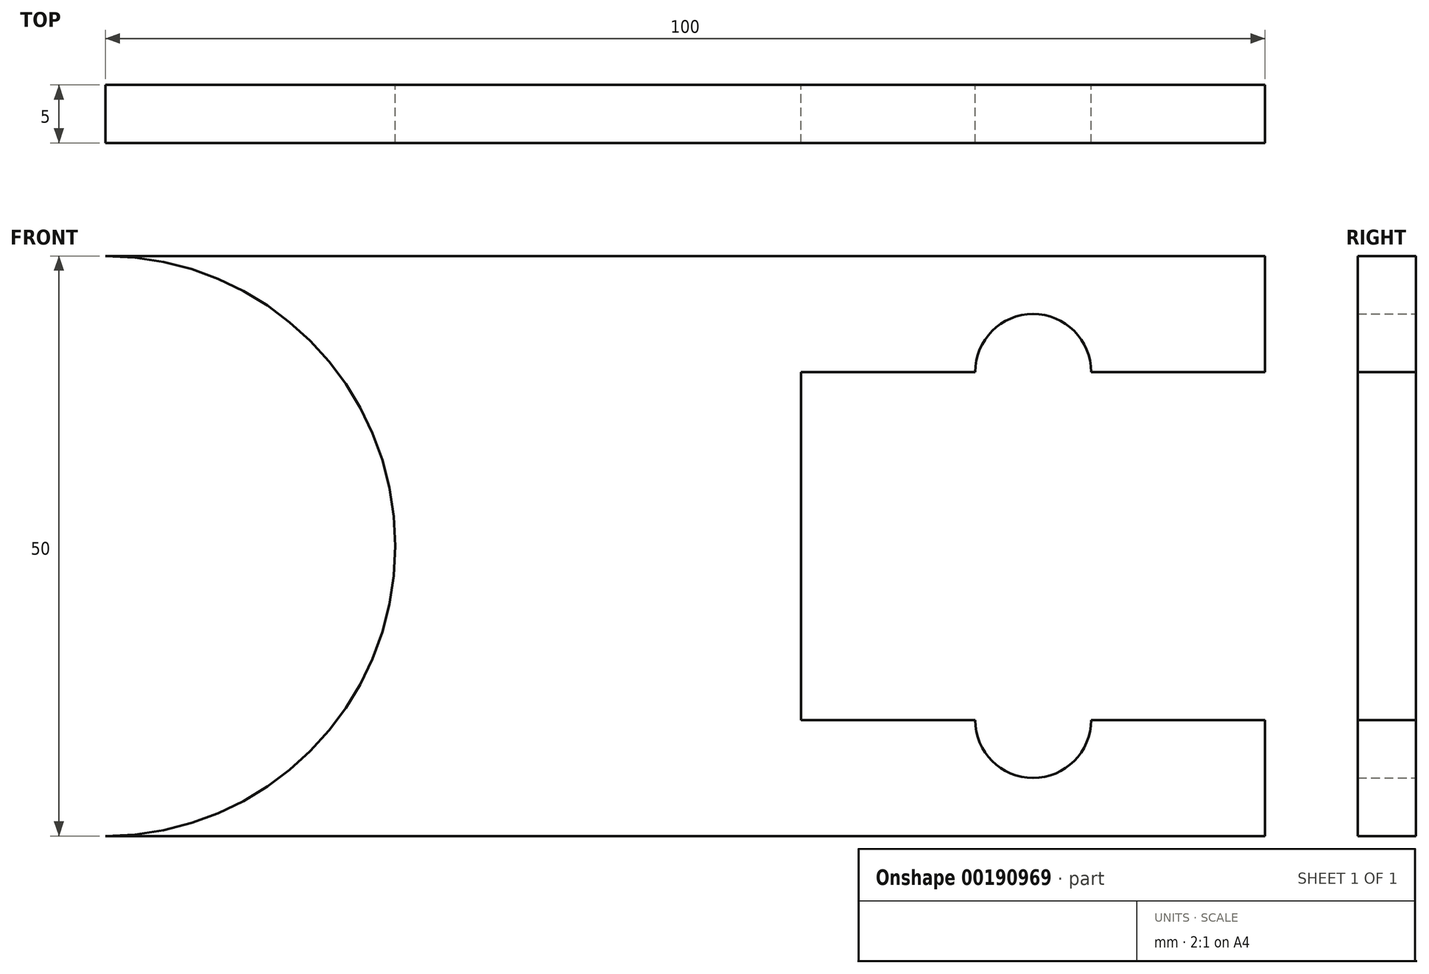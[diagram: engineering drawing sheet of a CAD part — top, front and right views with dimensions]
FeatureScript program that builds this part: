
annotation { "Feature Type Name" : "Feature", "Feature Type Description" : "" }
export const myFeature = defineFeature(function(context is Context, id is Id, definition is map)
    precondition{}
    {
        {
            var Q0;
            Q0=qCreatedBy(makeId("Front.planeOp"),FACE);
            var sketch = newSketch(context, id + "F0", { "sketchPlane" : qUnion([Q0])});
            skLineSegment(sketch, "E0.bottom", {"start": v(0, 0) * mm, "end": v(40, 0) * mm});
            skLineSegment(sketch, "E0.top", {"start": v(0, 50) * mm, "end": v(40, 50) * mm});
            skLineSegment(sketch, "E0.left", {"start": v(0, 0) * mm, "end": v(0, 50) * mm});
            skLineSegment(sketch, "E0.right", {"start": v(40, 0) * mm, "end": v(40, 50) * mm});
            skLineSegment(sketch, "E1.bottom", {"start": v(-60, 10) * mm, "end": v(40, 10) * mm});
            skLineSegment(sketch, "E1.top", {"start": v(-60, 40) * mm, "end": v(40, 40) * mm});
            skLineSegment(sketch, "E1.left", {"start": v(-60, 10) * mm, "end": v(-60, 40) * mm});
            skLineSegment(sketch, "E1.right", {"start": v(40, 10) * mm, "end": v(40, 40) * mm});
            skArc(sketch, "E2", {"start": v(-60, 40) * mm, "mid": v(-45, 25) * mm, "end": v(-60, 10) * mm});
            skCircle(sketch, "E3", {"center": v(20, 40) * mm, "radius": 5 * mm});
            skCircle(sketch, "E4", {"center": v(20, 10) * mm, "radius": 5 * mm});
            skLineSegment(sketch, "E5.bottom", {"start": v(0, 50) * mm, "end": v(-60, 50) * mm});
            skLineSegment(sketch, "E5.top", {"start": v(0, 0) * mm, "end": v(-60, 0) * mm});
            skLineSegment(sketch, "E5.left", {"start": v(0, 50) * mm, "end": v(0, 0) * mm});
            skLineSegment(sketch, "E5.right", {"start": v(-60, 50) * mm, "end": v(-60, 0) * mm});
            skCircle(sketch, "E6", {"center": v(-60, 25) * mm, "radius": 25 * mm});
            skSolve(sketch);
        }
        {
            var Q0;
            {var subQ5=sQuery(id+"F0.wireOp",EDGE,"E1.right");Q0=makeQuery(id+"F0.imprint","IMPRINT",FACE,{"disambiguationData":[TD([[makeQuery(id+"F0.imprint","IMPRINT",EDGE,{"derivedFrom":subQ5}),1.0]])]});}
            var Q1;
            {var subQ6=sQuery(id+"F0.wireOp",EDGE,"E0.top");Q1=makeQuery(id+"F0.imprint","IMPRINT",FACE,{"disambiguationData":[TD([[makeQuery(id+"F0.imprint","IMPRINT",EDGE,{"derivedFrom":subQ6}),-1.0]])]});}
            var Q2;
            {var subQ7=sQuery(id+"F0.wireOp",EDGE,"E0.bottom");Q2=makeQuery(id+"F0.imprint","IMPRINT",FACE,{"disambiguationData":[TD([[makeQuery(id+"F0.imprint","IMPRINT",EDGE,{"derivedFrom":subQ7}),1.0]])]});}
            var Q3;
            {var subQ0=sQuery(id+"F0.wireOp",EDGE,"E6");var subQ1=sQuery(id+"F0.wireOp",EDGE,"E1.bottom");var subQ2=makeQuery(id+"F0.imprint","INTERSECT",VERTEX,{"derivedFrom":[subQ1,subQ0]});Q3=makeQuery(id+"F0.imprint","IMPRINT",FACE,{"disambiguationData":[TD([[makeQuery(id+"F0.imprint","IMPRINT",EDGE,{"disambiguationData":[TD([[subQ2,-1.0]])],"derivedFrom":subQ1}),1.0]])]});}
            var Q4;
            {var subQ5=sQuery(id+"F0.wireOp",EDGE,"E5.bottom");Q4=makeQuery(id+"F0.imprint","IMPRINT",FACE,{"disambiguationData":[TD([[makeQuery(id+"F0.imprint","IMPRINT",EDGE,{"derivedFrom":subQ5}),1.0]])]});}
            var Q5;
            {var subQ5=sQuery(id+"F0.wireOp",EDGE,"E5.top");Q5=makeQuery(id+"F0.imprint","IMPRINT",FACE,{"disambiguationData":[TD([[makeQuery(id+"F0.imprint","IMPRINT",EDGE,{"derivedFrom":subQ5}),-1.0]])]});}
            extrude(context, id + "F1", {"entities" : qUnion([Q0, Q1, Q2, Q3, Q4, Q5]), "depth" : 5 * mm});
        }
    });
